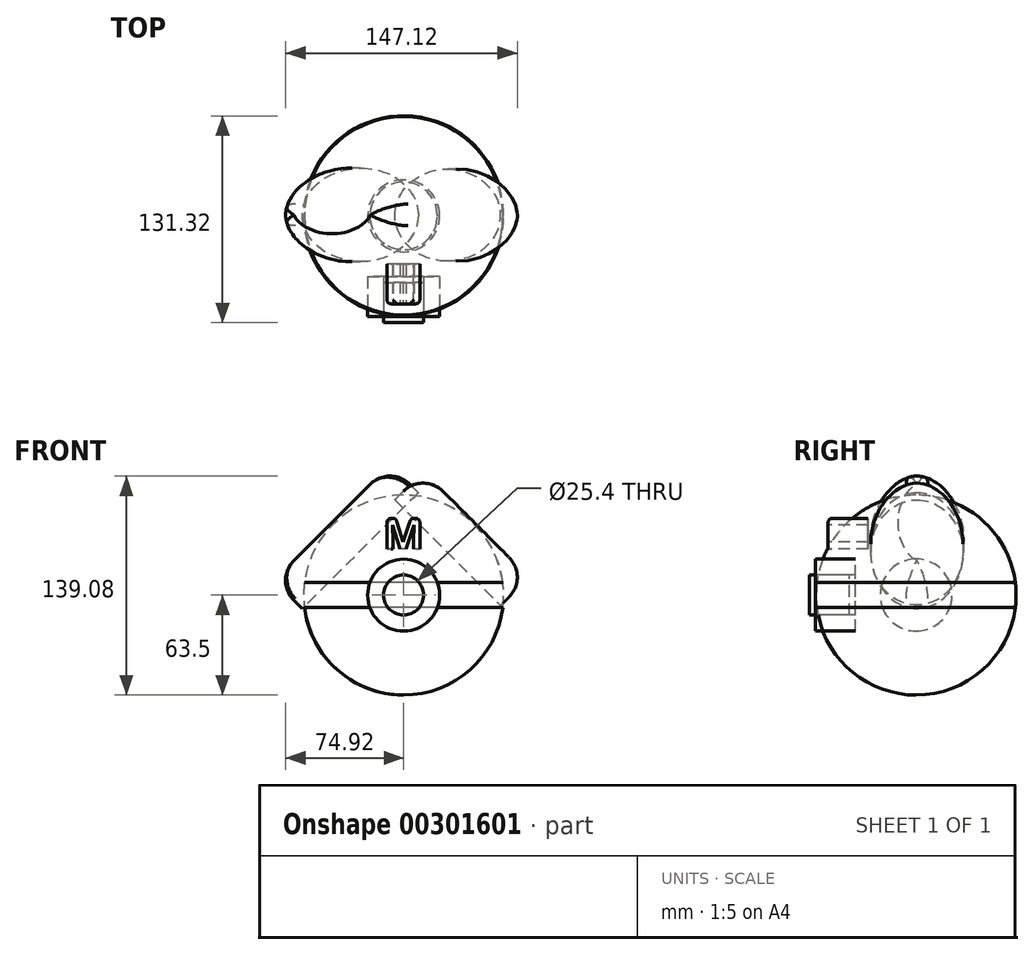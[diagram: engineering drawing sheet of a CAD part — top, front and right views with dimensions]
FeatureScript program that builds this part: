
annotation { "Feature Type Name" : "Feature", "Feature Type Description" : "" }
export const myFeature = defineFeature(function(context is Context, id is Id, definition is map)
    precondition{}
    {
        {
            var Q0;
            Q0=qCreatedBy(makeId("Front.planeOp"),FACE);
            var sketch = newSketch(context, id + "F0", { "sketchPlane" : qUnion([Q0])});
            skArc(sketch, "E0", {"start": v(0, 63.5) * mm, "mid": v(-63.5, 0) * mm, "end": v(0, -63.5) * mm});
            skPoint(sketch, "E1.start.orphan", {"position": v(0, 63.5) * mm});
            skLineSegment(sketch, "E2", {"start": v(0, 63.5) * mm, "end": v(0, -63.5) * mm, "construction": true});
            skLineSegment(sketch, "E3", {"start": v(0, 63.5) * mm, "end": v(0, -63.5) * mm});
            skLineSegment(sketch, "E4", {"start": v(-63, 7.9) * mm, "end": v(-21.45, 7.9) * mm});
            skLineSegment(sketch, "E5", {"start": v(-63, -7.87) * mm, "end": v(-21.46, -7.87) * mm});
            skLineSegment(sketch, "E6", {"start": v(-21.45, 7.9) * mm, "end": v(0, 7.9) * mm});
            skLineSegment(sketch, "E7", {"start": v(-21.46, -7.87) * mm, "end": v(0, -7.87) * mm});
            skCircle(sketch, "E8", {"center": v(0, 0) * mm, "radius": 22.86 * mm});
            skCircle(sketch, "E9.0", {"center": v(0, 0) * mm, "radius": 13.97 * mm});
            skSolve(sketch);
        }
        {
            var Q0;
            {var subQ3=sQuery(id+"F0.wireOp",EDGE,"E4");Q0=makeQuery(id+"F0.imprint","IMPRINT",FACE,{"disambiguationData":[TD([[makeQuery(id+"F0.imprint","IMPRINT",EDGE,{"derivedFrom":subQ3}),1.0]])]});}
            var Q1;
            Q1=sQuery(id+"F0.wireOp",EDGE,"E3");
            revolve(context, id + "F1", {"entities" : qUnion([Q0]), "axis" : qUnion([Q1]), "revolveType" : RevolveType.FULL});
        }
        {
            var Q0;
            {var subQ3=sQuery(id+"F0.wireOp",EDGE,"E5");Q0=makeQuery(id+"F0.imprint","IMPRINT",FACE,{"disambiguationData":[TD([[makeQuery(id+"F0.imprint","IMPRINT",EDGE,{"derivedFrom":subQ3}),-1.0]])]});}
            var Q1;
            Q1=sQuery(id+"F0.wireOp",EDGE,"E3");
            revolve(context, id + "F2", {"entities" : qUnion([Q0]), "axis" : qUnion([Q1]), "revolveType" : RevolveType.FULL});
        }
        {
            var Q0;
            {var subQ0=sQuery(id+"F0.wireOp",EDGE,"E4");Q0=makeQuery(id+"F0.imprint","IMPRINT",FACE,{"disambiguationData":[TD([[makeQuery(id+"F0.imprint","IMPRINT",EDGE,{"derivedFrom":subQ0}),-1.0]])]});}
            var Q1;
            Q1=sQuery(id+"F0.wireOp",EDGE,"E3");
            revolve(context, id + "F3", {"entities" : qUnion([Q0]), "axis" : qUnion([Q1]), "revolveType" : RevolveType.FULL});
        }
        {
            var Q0;
            Q0=qCreatedBy(makeId("Front.planeOp"),FACE);
            cPlane(context, id + "F4", {"entities" : qUnion([Q0]), "cplaneType" : CPlaneType.OFFSET, "offset" : 64 * mm, "width" : 152.4 * mm, "height" : 152.4 * mm});
        }
        {
            var Q0;
            Q0=qCreatedBy(id+"F4.planeOp",FACE);
            var sketch = newSketch(context, id + "F5", { "sketchPlane" : qUnion([Q0])});
            skCircle(sketch, "E10", {"center": v(0, 0) * mm, "radius": 22.86 * mm});
            skCircle(sketch, "E11", {"center": v(0, 0) * mm, "radius": 12.7 * mm});
            skSolve(sketch);
        }
        {
            var Q0;
            Q0=makeQuery(id+"F5.imprint","IMPRINT",FACE,{"disambiguationData":[TD([[makeQuery(id+"F5.imprint","IMPRINT",EDGE,{"derivedFrom":sQuery(id+"F5.wireOp",EDGE,"E10")}),1.0]])]});
            extrude(context, id + "F6", {"entities" : qUnion([Q0]), "oppositeDirection" : true, "depth" : 25.4 * mm});
        }
        {
            var Q0;
            Q0=qCreatedBy(id+"F4.planeOp",FACE);
            cPlane(context, id + "F7", {"entities" : qUnion([Q0]), "cplaneType" : CPlaneType.OFFSET, "offset" : 3.8 * mm, "width" : 152.4 * mm, "height" : 152.4 * mm});
        }
        {
            var Q0;
            Q0=qCreatedBy(id+"F7.planeOp",FACE);
            var sketch = newSketch(context, id + "F8", { "sketchPlane" : qUnion([Q0])});
            skCircle(sketch, "E12", {"center": v(0, 0) * mm, "radius": 12.7 * mm});
            skSolve(sketch);
        }
        {
            var Q0;
            Q0=makeQuery(id+"F8.imprint","IMPRINT",FACE,{"disambiguationData":[TD([[makeQuery(id+"F8.imprint","IMPRINT",EDGE,{"derivedFrom":sQuery(id+"F8.wireOp",EDGE,"E12")}),1.0]])]});
            extrude(context, id + "F9", {"entities" : qUnion([Q0]), "oppositeDirection" : true, "depth" : 25.4 * mm});
        }
        {
            var Q0;
            Q0=qCreatedBy(makeId("Front.planeOp"),FACE);
            cPlane(context, id + "F10", {"entities" : qUnion([Q0]), "cplaneType" : CPlaneType.OFFSET, "offset" : 55.88 * mm, "width" : 152.4 * mm, "height" : 152.4 * mm});
        }
        {
            var Q0;
            Q0=qCreatedBy(id+"F10.planeOp",FACE);
            var sketch = newSketch(context, id + "F11", { "sketchPlane" : qUnion([Q0])});
            skText(sketch, "E13", { "text": "M", "fontName": "OpenSans-Bold.ttf"});
            const initialGuessF11  = {"E13": [-0.01303, 0.02924, 1, 0, 0.01969]};
            skSetInitialGuess(sketch, initialGuessF11);
            skSolve(sketch);
        }
        {
            var Q0;
            Q0 = qSketchRegion(id + "F11", true);
            extrude(context, id + "F12", {"entities" : qUnion([Q0]), "oppositeDirection" : true, "depth" : 25.4 * mm});
        }
        {
            var Q0;
            Q0=makeQuery(id+"F12.opExtrude","CAP_EDGE",EDGE,{"disambiguationData":[OSD([sQuery(id+"F11.wireOp",EDGE,"E13.sketch_text.stroke-10")])],"isStart":true});
            var Q1;
            Q1=makeQuery(id+"F12.opExtrude","CAP_EDGE",EDGE,{"disambiguationData":[OSD([sQuery(id+"F11.wireOp",EDGE,"E13.sketch_text.stroke-6")])],"isStart":true});
            var Q2;
            Q2=makeQuery(id+"F12.opExtrude","CAP_EDGE",EDGE,{"disambiguationData":[OSD([sQuery(id+"F11.wireOp",EDGE,"E13.sketch_text.stroke-11")])],"isStart":true});
            var Q3;
            Q3=makeQuery(id+"F12.opExtrude","CAP_EDGE",EDGE,{"disambiguationData":[OSD([sQuery(id+"F11.wireOp",EDGE,"E13.sketch_text.stroke-5")])],"isStart":true});
            var Q4;
            Q4=makeQuery(id+"F12.opExtrude","SWEPT_EDGE",EDGE,{"disambiguationData":[OSD([sQuery(id+"F11.wireOp",EDGE,"E13.sketch_text.stroke-10"),sQuery(id+"F11.wireOp",EDGE,"E13.sketch_text.stroke-11")])]});
            var Q5;
            Q5=makeQuery(id+"F12.opExtrude","SWEPT_EDGE",EDGE,{"disambiguationData":[OSD([sQuery(id+"F11.wireOp",EDGE,"E13.sketch_text.stroke-9"),sQuery(id+"F11.wireOp",EDGE,"E13.sketch_text.stroke-10")])]});
            var Q6;
            Q6=makeQuery(id+"F12.opExtrude","SWEPT_EDGE",EDGE,{"disambiguationData":[OSD([sQuery(id+"F11.wireOp",EDGE,"E13.sketch_text.stroke-5"),sQuery(id+"F11.wireOp",EDGE,"E13.sketch_text.stroke-6")])]});
            var Q7;
            Q7=makeQuery(id+"F12.opExtrude","SWEPT_EDGE",EDGE,{"disambiguationData":[OSD([sQuery(id+"F11.wireOp",EDGE,"E13.sketch_text.stroke-6"),sQuery(id+"F11.wireOp",EDGE,"E13.sketch_text.stroke-7")])]});
            fillet(context, id + "F13", {"entities" : qUnion([Q0, Q1, Q2, Q3, Q4, Q5, Q6, Q7]), "radius" : 2.54 * mm, "tangentPropagation" : true, "allowEdgeOverflow" : false});
        }
        {
            var Q0;
            Q0=qCreatedBy(makeId("Top.planeOp"),FACE);
            cPlane(context, id + "F14", {"entities" : qUnion([Q0]), "cplaneType" : CPlaneType.OFFSET, "offset" : 59.69 * mm, "width" : 152.4 * mm, "height" : 152.4 * mm});
        }
        {
            var Q0;
            Q0=qCreatedBy(makeId("Top.planeOp"),FACE);
            var sketch = newSketch(context, id + "F15", { "sketchPlane" : qUnion([Q0])});
            skLineSegment(sketch, "E14", {"start": v(0, 76.88) * mm, "end": v(0, -76.88) * mm, "construction": true});
            skSolve(sketch);
        }
        {
            var Q0;
            Q0=qCreatedBy(makeId("Top.planeOp"),FACE);
            var Q1;
            Q1=sQuery(id+"F15.wireOp",EDGE,"E14");
            cPlane(context, id + "F16", {"entities" : qUnion([Q0, Q1]), "cplaneType" : CPlaneType.LINE_ANGLE, "offset" : 25.4 * mm, "angle" : 45 * degree, "oppositeDirection" : true, "width" : 152.4 * mm, "height" : 152.4 * mm});
        }
        {
            var Q0;
            Q0=qCreatedBy(id+"F16.planeOp",FACE);
            cPlane(context, id + "F17", {"entities" : qUnion([Q0]), "cplaneType" : CPlaneType.OFFSET, "offset" : 64.26 * mm, "oppositeDirection" : true, "width" : 152.4 * mm, "height" : 152.4 * mm});
        }
        {
            var Q0;
            Q0=qCreatedBy(id+"F17.planeOp",FACE);
            var sketch = newSketch(context, id + "F18", { "sketchPlane" : qUnion([Q0])});
            skEllipse(sketch, "E15", {"center": v(-0.44, -0.75) * mm, "majorRadius": 47.51 * mm, "minorRadius": 29.31 * mm, "majorAxis": v(0, 1)});
            skSolve(sketch);
        }
        {
            var Q0;
            Q0 = qSketchRegion(id + "F18", true);
            extrude(context, id + "F19", {"entities" : qUnion([Q0]), "depth" : 25.4 * mm});
        }
        {
            var Q0;
            Q0=makeQuery(id+"F19.opExtrude","CAP_EDGE",EDGE,{"disambiguationData":[OSD([sQuery(id+"F18.wireOp",EDGE,"E15")])],"isStart":true});
            fillet(context, id + "F20", {"entities" : qUnion([Q0]), "radius" : 17.78 * mm, "tangentPropagation" : true, "allowEdgeOverflow" : false});
        }
        {
            var Q0;
            Q0=qCreatedBy(makeId("Top.planeOp"),FACE);
            var Q1;
            Q1=sQuery(id+"F15.wireOp",EDGE,"E14");
            cPlane(context, id + "F21", {"entities" : qUnion([Q0, Q1]), "cplaneType" : CPlaneType.LINE_ANGLE, "offset" : 25.4 * mm, "angle" : 45 * degree, "width" : 152.4 * mm, "height" : 152.4 * mm});
        }
        {
            var Q0;
            Q0=qCreatedBy(id+"F21.planeOp",FACE);
            cPlane(context, id + "F22", {"entities" : qUnion([Q0]), "cplaneType" : CPlaneType.OFFSET, "offset" : 64.77 * mm, "oppositeDirection" : true, "width" : 152.4 * mm, "height" : 152.4 * mm});
        }
        {
            var Q0;
            Q0=qCreatedBy(id+"F22.planeOp",FACE);
            var sketch = newSketch(context, id + "F23", { "sketchPlane" : qUnion([Q0])});
            skEllipse(sketch, "E16", {"center": v(0.6, 0.47) * mm, "majorRadius": 52.1 * mm, "minorRadius": 29.8 * mm, "majorAxis": v(0, 1)});
            skSolve(sketch);
        }
        {
            var Q0;
            Q0 = qSketchRegion(id + "F23", true);
            extrude(context, id + "F24", {"entities" : qUnion([Q0]), "depth" : 25.4 * mm});
        }
        {
            var Q0;
            Q0=makeQuery(id+"F24.opExtrude","CAP_EDGE",EDGE,{"disambiguationData":[OSD([sQuery(id+"F23.wireOp",EDGE,"E16")])],"isStart":true});
            fillet(context, id + "F25", {"entities" : qUnion([Q0]), "radius" : 17.78 * mm, "tangentPropagation" : true, "allowEdgeOverflow" : false});
        }
    });
